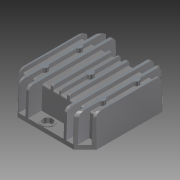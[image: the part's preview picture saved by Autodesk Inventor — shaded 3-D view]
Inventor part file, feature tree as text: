
AUTODESK INVENTOR PART (.ipt)
format: ipt  version: 2013 (Build 170138000, 138)  size: 353,280 bytes
history: native  units: in
note: dims shown in document units (in); Inventor stores cm internally (conversion verified against a paired STEP export)
features: extrude x8, sketch x7, plane x3, fillet x3, mirror x2, projected_geometry x1
ambient origin geometry x8: Origin, YZ Plane, XZ Plane, XY Plane, X Axis, Y Axis, Z Axis, Center Point
bodies: Solid1 (feature_tree)
feature tree (24):
  sketch  "Sketch1"  dims[d0=0.906in d1=-0.0137in d4=0.25in d5=0.25in]
  extrude  "Extrusion1"  Depth=0.25in
  extrude  "Extrusion3"  Depth=0.047in
  plane  "Work Plane1"
  mirror  "Mirror1"
  plane  "Work Plane2"
  extrude  "Extrusion4"  Depth=0.079in
  extrude  "Extrusion5"  Depth=0.079in
  extrude  "Extrusion6"  Depth=0.2403in
  extrude  "Extrusion7"  TaperAngle=0.0deg  [1 undecoded]
  fillet  "Fillet1"  Radius=0.787in
  fillet  "Fillet2"  Radius=0.787in
  fillet  "Fillet3"  Radius=0.787in
  extrude  "Extrusion8"  Depth=0.125in
  plane  "Work Plane3"
  mirror  "Mirror2"
  extrude  "Extrusion9"  Depth=0.05in
  sketch  "Sketch4"  dims[d6=0.25in d7=0.047in]
  sketch  "Sketch5"  dims[d8=0.202in d9=0.079in]
  sketch  "Sketch7"  dims[d10=0.202in d11=0.079in]
  sketch  "Sketch8"  dims[d12=0.787in d13=0.0in d14=0.2403in]
  sketch  "Sketch9"  dims[d16=0.182in d17=0.0in d18=0.787in d19=0.0in d20=0.787in d21=0.0in d22=0.787in d23=0.0in]
  projected_geometry  "Projected Loop1"
  sketch  "Sketch10"  dims[d24=0.787in d25=0.0in d26=0.125in d27=0.05in d28=0.05in d29=0.2in d32=1.0in d33=0.787in d34=0.0in d35=0.375in d37=0.02in d38=-0.0137in]
note: 1 required parameter value undecoded (feature->parameter linkage not recoverable at this tier; creation-order binding heuristic only, values carry confidence <= 0.55)
